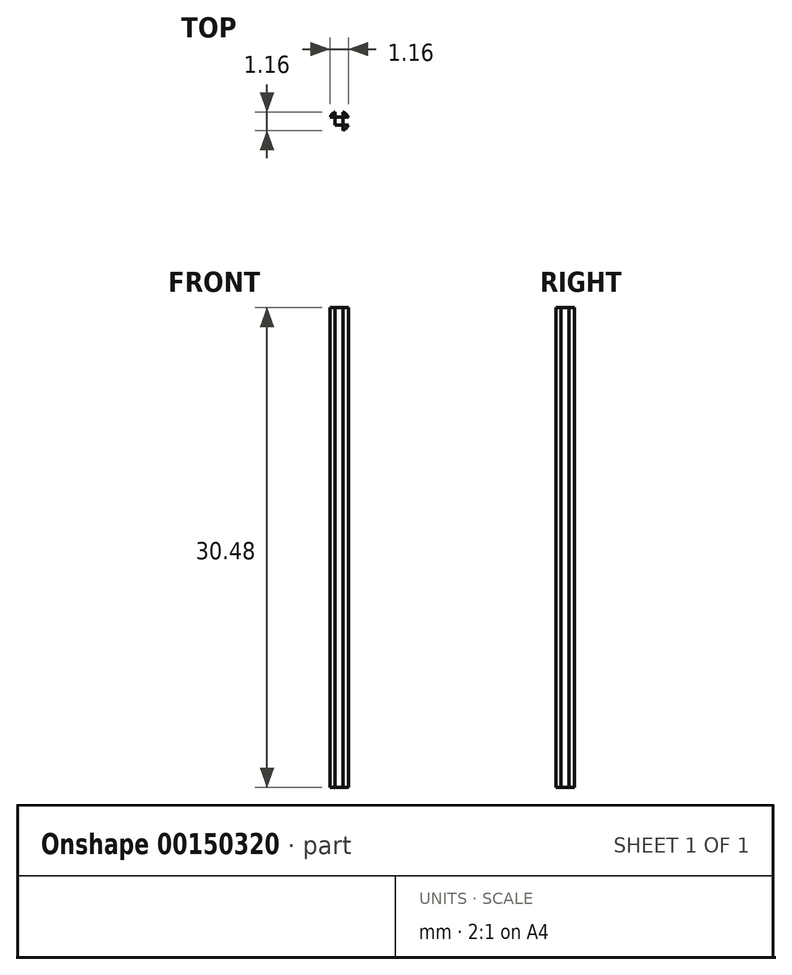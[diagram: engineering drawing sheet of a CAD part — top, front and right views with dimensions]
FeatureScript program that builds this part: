
annotation { "Feature Type Name" : "Feature", "Feature Type Description" : "" }
export const myFeature = defineFeature(function(context is Context, id is Id, definition is map)
    precondition{}
    {
        {
            var Q0;
            Q0=qCreatedBy(makeId("Top.planeOp"),FACE);
            var sketch = newSketch(context, id + "F0", { "sketchPlane" : qUnion([Q0])});
            skCircle(sketch, "E0", {"center": v(0, 0) * mm, "radius": 0.64 * mm});
            skLineSegment(sketch, "E1.bottom", {"start": v(1.1, 0.25) * mm, "end": v(-1.1, 0.25) * mm});
            skLineSegment(sketch, "E1.top", {"start": v(1.1, -0.25) * mm, "end": v(-1.1, -0.25) * mm});
            skLineSegment(sketch, "E1.left", {"start": v(1.1, 0.25) * mm, "end": v(1.1, -0.25) * mm});
            skLineSegment(sketch, "E1.right", {"start": v(-1.1, 0.25) * mm, "end": v(-1.1, -0.25) * mm});
            skLineSegment(sketch, "E2.bottom", {"start": v(-0.25, 1.25) * mm, "end": v(0.25, 1.25) * mm});
            skLineSegment(sketch, "E2.top", {"start": v(-0.25, -1.25) * mm, "end": v(0.25, -1.25) * mm});
            skLineSegment(sketch, "E2.left", {"start": v(-0.25, 1.25) * mm, "end": v(-0.25, -1.25) * mm});
            skLineSegment(sketch, "E2.right", {"start": v(0.25, 1.25) * mm, "end": v(0.25, -1.25) * mm});
            skSolve(sketch);
        }
        {
            var Q0;
            {var subQ0=sQuery(id+"F0.wireOp",EDGE,"E2.right");var subQ1=sQuery(id+"F0.wireOp",EDGE,"E0");var subQ2=makeQuery(id+"F0.imprint","INTERSECT",VERTEX,{"disambiguationData":[OD(0.0)],"derivedFrom":[subQ1,subQ0]});Q0=makeQuery(id+"F0.imprint","IMPRINT",FACE,{"disambiguationData":[TD([[makeQuery(id+"F0.imprint","IMPRINT",EDGE,{"disambiguationData":[TD([[subQ2,-1.0]])],"derivedFrom":subQ1}),1.0]])]});}
            var Q1;
            {var subQ0=sQuery(id+"F0.wireOp",EDGE,"E1.bottom");var subQ1=sQuery(id+"F0.wireOp",EDGE,"E0");var subQ2=makeQuery(id+"F0.imprint","INTERSECT",VERTEX,{"disambiguationData":[OD(1.0)],"derivedFrom":[subQ1,subQ0]});Q1=makeQuery(id+"F0.imprint","IMPRINT",FACE,{"disambiguationData":[TD([[makeQuery(id+"F0.imprint","IMPRINT",EDGE,{"disambiguationData":[TD([[subQ2,-1.0]])],"derivedFrom":subQ1}),1.0]])]});}
            var Q2;
            {var subQ0=sQuery(id+"F0.wireOp",EDGE,"E2.right");var subQ1=sQuery(id+"F0.wireOp",EDGE,"E1.bottom");var subQ2=makeQuery(id+"F0.imprint","INTERSECT",VERTEX,{"derivedFrom":[subQ1,subQ0]});Q2=makeQuery(id+"F0.imprint","IMPRINT",FACE,{"disambiguationData":[TD([[makeQuery(id+"F0.imprint","IMPRINT",EDGE,{"disambiguationData":[TD([[subQ2,-1.0]])],"derivedFrom":subQ1}),1.0]])]});}
            var Q3;
            {var subQ0=sQuery(id+"F0.wireOp",EDGE,"E1.bottom");var subQ1=sQuery(id+"F0.wireOp",EDGE,"E0");var subQ2=makeQuery(id+"F0.imprint","INTERSECT",VERTEX,{"disambiguationData":[OD(0.0)],"derivedFrom":[subQ1,subQ0]});Q3=makeQuery(id+"F0.imprint","IMPRINT",FACE,{"disambiguationData":[TD([[makeQuery(id+"F0.imprint","IMPRINT",EDGE,{"disambiguationData":[TD([[subQ2,1.0]])],"derivedFrom":subQ1}),1.0]])]});}
            var Q4;
            {var subQ0=sQuery(id+"F0.wireOp",EDGE,"E2.left");var subQ1=sQuery(id+"F0.wireOp",EDGE,"E0");var subQ2=makeQuery(id+"F0.imprint","INTERSECT",VERTEX,{"disambiguationData":[OD(1.0)],"derivedFrom":[subQ1,subQ0]});Q4=makeQuery(id+"F0.imprint","IMPRINT",FACE,{"disambiguationData":[TD([[makeQuery(id+"F0.imprint","IMPRINT",EDGE,{"disambiguationData":[TD([[subQ2,-1.0]])],"derivedFrom":subQ1}),1.0]])]});}
            extrude(context, id + "F1", {"entities" : qUnion([Q0, Q1, Q2, Q3, Q4]), "depth" : 30.48 * mm});
        }
    });
